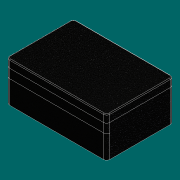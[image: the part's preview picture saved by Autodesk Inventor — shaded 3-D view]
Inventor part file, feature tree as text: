
AUTODESK INVENTOR PART (.ipt)
format: ipt  version: 2017 (Build 210142000, 142)  size: 125,440 bytes
history: native  units: in
note: dims shown in document units (in); Inventor stores cm internally (conversion verified against a paired STEP export)
features: plane x2, split x2, fillet x2, extrude x1, sketch x1
ambient origin geometry x8: Origin, YZ Plane, XZ Plane, XY Plane, X Axis, Y Axis, Z Axis, Center Point
bodies: Solid1 (feature_tree)
feature tree (8):
  extrude  "Extrusion1"  Depth=20.375in
  plane  "Work Plane1"
  split  "Split1"
  plane  "Work Plane2"
  split  "Split2"
  fillet  "Fillet1"  Radius=12.125in
  fillet  "Fillet2"  Radius=9.75in
  sketch  "Sketch1"  dims[d0=30.5in d1=20.375in d2=12.125in d3=0.0in d4=9.75in d5=7.0in d6=1.0in d7=0.25in]
